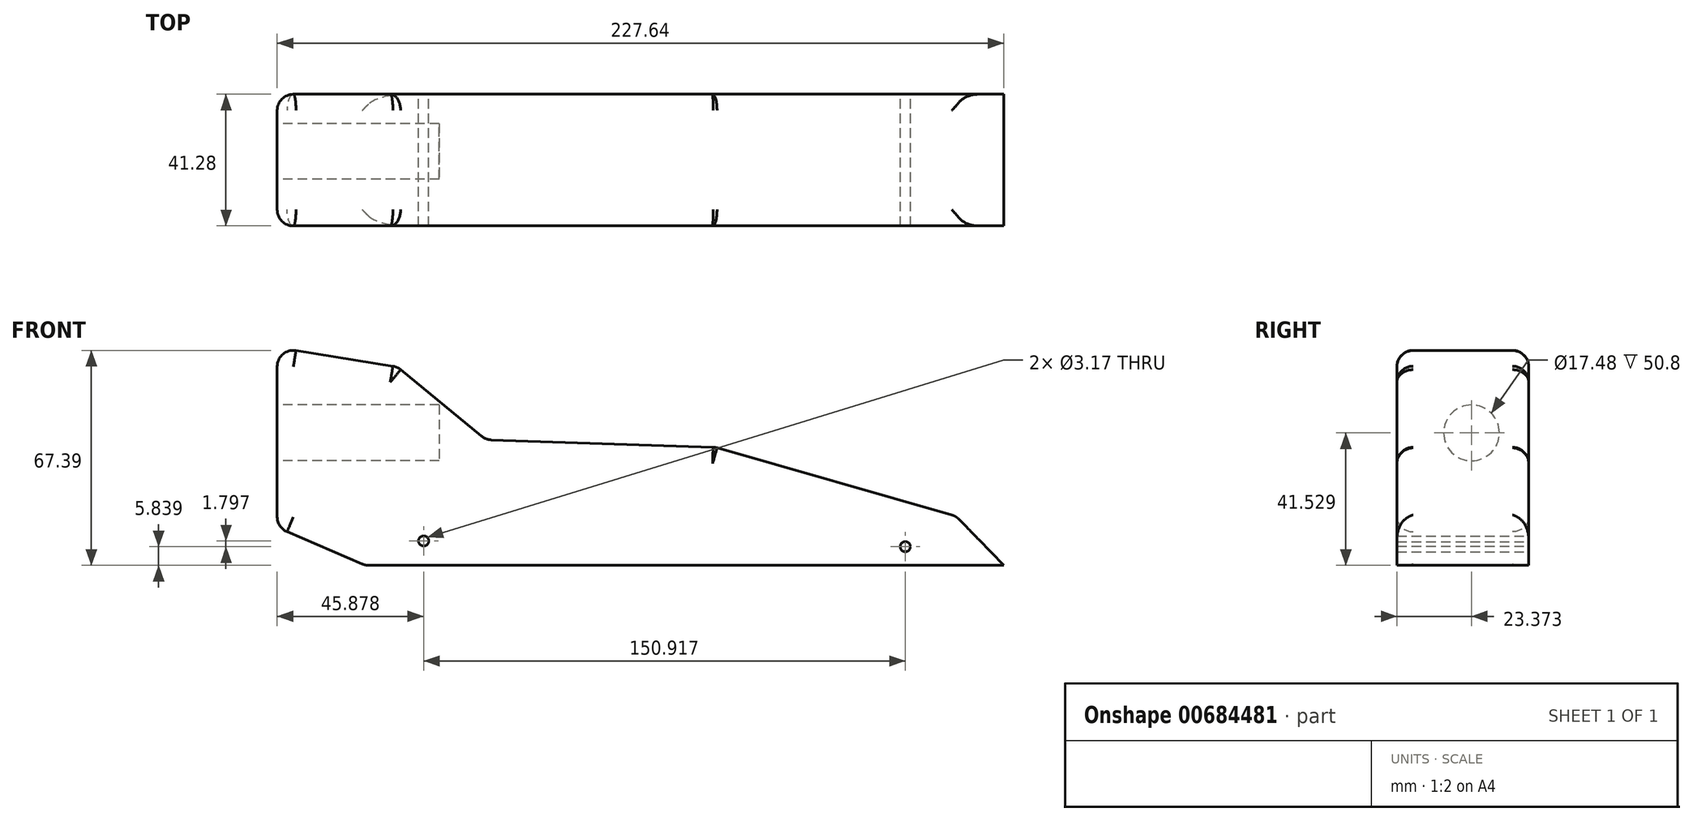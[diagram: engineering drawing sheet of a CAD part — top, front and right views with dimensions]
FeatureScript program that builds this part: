
annotation { "Feature Type Name" : "Feature", "Feature Type Description" : "" }
export const myFeature = defineFeature(function(context is Context, id is Id, definition is map)
    precondition{}
    {
        {
            var Q0;
            Q0=qCreatedBy(makeId("Front.planeOp"),FACE);
            var sketch = newSketch(context, id + "F0", { "sketchPlane" : qUnion([Q0])});
            skLineSegment(sketch, "E0", {"start": v(0, 0) * mm, "end": v(304.8, 0) * mm});
            skLineSegment(sketch, "E1", {"start": v(304.8, 0) * mm, "end": v(304.8, 19.05) * mm});
            skLineSegment(sketch, "E2", {"start": v(304.8, 19.05) * mm, "end": v(0, 68.28) * mm});
            skLineSegment(sketch, "E3", {"start": v(0, 68.28) * mm, "end": v(0, 0) * mm});
            skSolve(sketch);
        }
        {
            var Q0;
            Q0 = qSketchRegion(id + "F0", true);
            extrude(context, id + "F1", {"entities" : qUnion([Q0]), "depth" : 41.27 * mm, "offsetDistance" : 25.4 * mm});
        }
        {
            var Q0;
            Q0=makeQuery(id+"F1.opExtrude","CAP_FACE",FACE,{"disambiguationData":[OSD([sQuery(id+"F0.wireOp",EDGE,"E0"),sQuery(id+"F0.wireOp",EDGE,"E1"),sQuery(id+"F0.wireOp",EDGE,"E2"),sQuery(id+"F0.wireOp",EDGE,"E3")])],"isStart":false});
            var sketch = newSketch(context, id + "F2", { "sketchPlane" : qUnion([Q0])});
            skSolve(sketch);
        }
        {
            var Q0;
            Q0=makeQuery(id+"F2.imprint","IMPRINT",FACE,{"disambiguationData":[TD([[makeQuery(id+"F2.imprint","IMPRINT",EDGE,{"derivedFrom":makeQuery(id+"F1.opExtrude","CAP_EDGE",EDGE,{"disambiguationData":[OSD([sQuery(id+"F0.wireOp",EDGE,"E0")])],"isStart":false})}),1.0]])]});
            var sketch = newSketch(context, id + "F3", { "sketchPlane" : qUnion([Q0])});
            skLineSegment(sketch, "E4", {"start": v(36.6, 63.03) * mm, "end": v(65.34, 39.38) * mm});
            skLineSegment(sketch, "E5", {"start": v(65.34, 39.38) * mm, "end": v(137.2, 36.98) * mm});
            skLineSegment(sketch, "E6", {"start": v(137.2, 36.98) * mm, "end": v(212.67, 15.42) * mm});
            skLineSegment(sketch, "E7", {"start": v(212.67, 15.42) * mm, "end": v(227.64, 0) * mm});
            skLineSegment(sketch, "E8", {"start": v(227.64, 0) * mm, "end": v(27.61, 0) * mm});
            skLineSegment(sketch, "E9", {"start": v(27.61, 0) * mm, "end": v(0, 11.83) * mm});
            skLineSegment(sketch, "E10", {"start": v(0, 11.83) * mm, "end": v(0, 67.93) * mm});
            skLineSegment(sketch, "E11", {"start": v(0, 67.93) * mm, "end": v(36.6, 63.03) * mm});
            skSolve(sketch);
        }
        {
            var Q0;
            {var subQ1=sQuery(id+"F3.wireOp",EDGE,"E5");Q0=makeQuery(id+"F3.imprint","IMPRINT",FACE,{"disambiguationData":[TD([[makeQuery(id+"F3.imprint","IMPRINT",EDGE,{"derivedFrom":subQ1}),1.0]])]});}
            var Q1;
            {var subQ0=sQuery(id+"F3.wireOp",EDGE,"E9");Q1=makeQuery(id+"F3.imprint","IMPRINT",FACE,{"disambiguationData":[TD([[makeQuery(id+"F3.imprint","IMPRINT",EDGE,{"derivedFrom":subQ0}),1.0]])]});}
            extrude(context, id + "F4", {"entities" : qUnion([Q0, Q1]), "operationType" : NewBodyOperationType.REMOVE, "oppositeDirection" : true, "depth" : 53.6 * mm, "offsetDistance" : 25.4 * mm});
        }
        {
            var Q0;
            Q0=makeQuery(id+"F4.boolean.opBoolean","COPY",FACE,{"derivedFrom":makeQuery(id+"F4.opExtrude","SWEPT_FACE",FACE,{"disambiguationData":[OSD([sQuery(id+"F3.wireOp",EDGE,"E4")])]})});
            fillet(context, id + "F5", {"entities" : qUnion([Q0]), "radius" : 5.08 * mm, "tangentPropagation" : true, "allowEdgeOverflow" : false});
        }
        {
            var Q0;
            Q0=makeQuery(id+"F1.opExtrude","SWEPT_FACE",FACE,{"disambiguationData":[OSD([sQuery(id+"F0.wireOp",EDGE,"E2")])]});
            fillet(context, id + "F6", {"entities" : qUnion([Q0]), "radius" : 5.08 * mm, "tangentPropagation" : true, "allowEdgeOverflow" : false});
        }
        {
            var Q0;
            Q0=makeQuery(id+"F4.boolean.opBoolean","COPY",FACE,{"derivedFrom":makeQuery(id+"F4.opExtrude","SWEPT_FACE",FACE,{"disambiguationData":[OSD([sQuery(id+"F3.wireOp",EDGE,"E5")])]})});
            fillet(context, id + "F7", {"entities" : qUnion([Q0]), "radius" : 5.08 * mm, "tangentPropagation" : true, "allowEdgeOverflow" : false});
        }
        {
            var Q0;
            Q0=makeQuery(id+"F4.boolean.opBoolean","COPY",FACE,{"derivedFrom":makeQuery(id+"F4.opExtrude","SWEPT_FACE",FACE,{"disambiguationData":[OSD([sQuery(id+"F3.wireOp",EDGE,"E6")])]})});
            fillet(context, id + "F8", {"entities" : qUnion([Q0]), "radius" : 5.08 * mm, "tangentPropagation" : true, "allowEdgeOverflow" : false});
        }
        {
            var Q0;
            Q0=makeQuery(id+"F4.boolean.opBoolean","COPY",FACE,{"derivedFrom":makeQuery(id+"F4.opExtrude","SWEPT_FACE",FACE,{"disambiguationData":[OSD([sQuery(id+"F3.wireOp",EDGE,"E9")])]})});
            fillet(context, id + "F9", {"entities" : qUnion([Q0]), "radius" : 5.08 * mm, "tangentPropagation" : true, "allowEdgeOverflow" : false});
        }
        {
            var Q0;
            Q0=makeQuery(id+"F1.opExtrude","SWEPT_FACE",FACE,{"disambiguationData":[OSD([sQuery(id+"F0.wireOp",EDGE,"E3")])]});
            fillet(context, id + "F10", {"entities" : qUnion([Q0]), "radius" : 5.08 * mm, "tangentPropagation" : true, "allowEdgeOverflow" : false});
        }
        {
            var Q0;
            Q0=makeQuery(id+"F1.opExtrude","CAP_FACE",FACE,{"disambiguationData":[OSD([sQuery(id+"F0.wireOp",EDGE,"E0"),sQuery(id+"F0.wireOp",EDGE,"E1"),sQuery(id+"F0.wireOp",EDGE,"E2"),sQuery(id+"F0.wireOp",EDGE,"E3")])],"isStart":true});
            var sketch = newSketch(context, id + "F11", { "sketchPlane" : qUnion([Q0])});
            skCircle(sketch, "E12", {"center": v(-196.8, 5.84) * mm, "radius": 1.59 * mm});
            skSolve(sketch);
        }
        {
            var Q0;
            Q0 = qSketchRegion(id + "F11", true);
            extrude(context, id + "F12", {"entities" : qUnion([Q0]), "operationType" : NewBodyOperationType.REMOVE, "oppositeDirection" : true, "depth" : 43.43 * mm, "offsetDistance" : 25.4 * mm});
        }
        {
            var Q0;
            Q0=makeQuery(id+"F1.opExtrude","CAP_FACE",FACE,{"disambiguationData":[OSD([sQuery(id+"F0.wireOp",EDGE,"E0"),sQuery(id+"F0.wireOp",EDGE,"E1"),sQuery(id+"F0.wireOp",EDGE,"E2"),sQuery(id+"F0.wireOp",EDGE,"E3")])],"isStart":true});
            var sketch = newSketch(context, id + "F13", { "sketchPlane" : qUnion([Q0])});
            skCircle(sketch, "E13", {"center": v(-45.88, 7.64) * mm, "radius": 1.59 * mm});
            skSolve(sketch);
        }
        {
            var Q0;
            Q0 = qSketchRegion(id + "F13", true);
            extrude(context, id + "F14", {"entities" : qUnion([Q0]), "operationType" : NewBodyOperationType.REMOVE, "oppositeDirection" : true, "depth" : 63.75 * mm, "offsetDistance" : 25.4 * mm});
        }
        {
            var Q0;
            Q0=makeQuery(id+"F1.opExtrude","SWEPT_FACE",FACE,{"disambiguationData":[OSD([sQuery(id+"F0.wireOp",EDGE,"E3")])]});
            var sketch = newSketch(context, id + "F15", { "sketchPlane" : qUnion([Q0])});
            skCircle(sketch, "E14", {"center": v(17.9, 41.53) * mm, "radius": 8.74 * mm});
            skSolve(sketch);
        }
        {
            var Q0;
            Q0=makeQuery(id+"F15.imprint","IMPRINT",FACE,{"disambiguationData":[TD([[makeQuery(id+"F15.imprint","IMPRINT",EDGE,{"derivedFrom":sQuery(id+"F15.wireOp",EDGE,"E14")}),1.0]])]});
            extrude(context, id + "F16", {"entities" : qUnion([Q0]), "operationType" : NewBodyOperationType.REMOVE, "oppositeDirection" : true, "depth" : 50.8 * mm, "offsetDistance" : 25.4 * mm});
        }
    });
